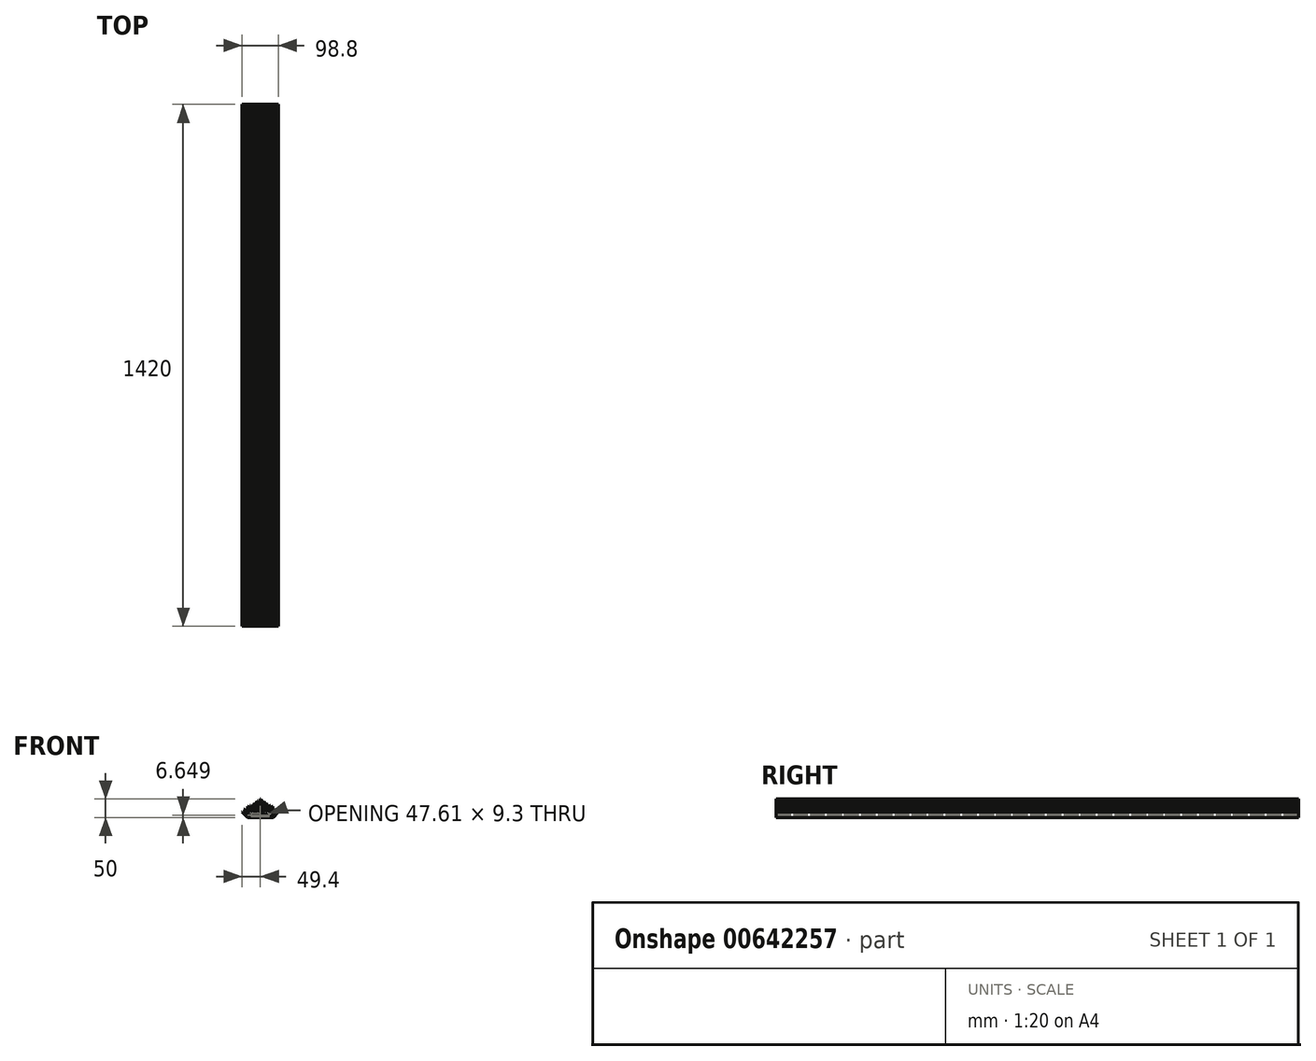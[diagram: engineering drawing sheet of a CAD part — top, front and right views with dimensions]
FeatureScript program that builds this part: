
annotation { "Feature Type Name" : "Feature", "Feature Type Description" : "" }
export const myFeature = defineFeature(function(context is Context, id is Id, definition is map)
    precondition{}
    {
        {
            var Q0;
            Q0=qCreatedBy(makeId("Front.planeOp"),FACE);
            var sketch = newSketch(context, id + "F0", { "sketchPlane" : qUnion([Q0])});
            skPoint(sketch, "E0.visualSharp", {"position": v(0, -3.5) * mm});
            skPoint(sketch, "E1.visualSharp", {"position": v(-32.72, 3.5) * mm});
            skLineSegment(sketch, "E2", {"start": v(-32.97, 18.5) * mm, "end": v(-34.47, 18.5) * mm});
            skLineSegment(sketch, "E3", {"start": v(-34.47, 18.5) * mm, "end": v(-34.72, 3.5) * mm});
            skLineSegment(sketch, "E4", {"start": v(-32.97, 18.5) * mm, "end": v(-32.72, 3.5) * mm});
            skLineSegment(sketch, "E5", {"start": v(-32.72, 3.5) * mm, "end": v(-28, 3.5) * mm});
            skLineSegment(sketch, "E6.1.0.0", {"start": v(-26.25, 21) * mm, "end": v(-26, 3.5) * mm});
            skLineSegment(sketch, "E6.1.0.2", {"start": v(-26, 3.5) * mm, "end": v(-21.24, 3.5) * mm});
            skPoint(sketch, "E6.1.0.3", {"position": v(-26, 3.5) * mm});
            skLineSegment(sketch, "E6.1.0.4", {"start": v(-26.25, 21) * mm, "end": v(-27.75, 21) * mm});
            skLineSegment(sketch, "E6.3.0.0", {"start": v(-12.87, 28.5) * mm, "end": v(-12.62, 3.5) * mm});
            skLineSegment(sketch, "E6.3.0.2", {"start": v(-12.62, 3.5) * mm, "end": v(-7.75, 3.5) * mm});
            skPoint(sketch, "E6.3.0.3", {"position": v(-12.62, 3.5) * mm});
            skLineSegment(sketch, "E6.3.0.4", {"start": v(-12.87, 28.5) * mm, "end": v(-14.37, 28.5) * mm});
            skLineSegment(sketch, "E6.4.0.0", {"start": v(-6, 33.5) * mm, "end": v(-5.75, 3.5) * mm});
            skLineSegment(sketch, "E6.4.0.2", {"start": v(-5.75, 3.5) * mm, "end": v(-1, 3.5) * mm});
            skPoint(sketch, "E6.4.0.3", {"position": v(-5.75, 3.5) * mm});
            skLineSegment(sketch, "E6.4.0.4", {"start": v(-6, 33.5) * mm, "end": v(-7.5, 33.5) * mm});
            skLineSegment(sketch, "E7", {"start": v(-27.75, 21) * mm, "end": v(-28, 3.5) * mm});
            skLineSegment(sketch, "E8", {"start": v(-20.99, 23.5) * mm, "end": v(-21.24, 3.5) * mm});
            skLineSegment(sketch, "E9", {"start": v(-0.75, 38.5) * mm, "end": v(-1, 3.5) * mm});
            skLineSegment(sketch, "E10", {"start": v(-7.75, 3.5) * mm, "end": v(-7.5, 33.5) * mm});
            skLineSegment(sketch, "E11", {"start": v(-14.37, 28.5) * mm, "end": v(-14.62, 3.5) * mm});
            skPoint(sketch, "E12", {"position": v(-34.72, 3.5) * mm});
            skLineSegment(sketch, "E13", {"start": v(0, -4.5) * mm, "end": v(-7.75, -4.5) * mm});
            skLineSegment(sketch, "E14", {"start": v(-34.72, 3.5) * mm, "end": v(-34.72, -11.5) * mm});
            skLineSegment(sketch, "E15", {"start": v(-7.75, -4.5) * mm, "end": v(-9.68, -2.2) * mm});
            skLineSegment(sketch, "E16", {"start": v(-11.21, -4.5) * mm, "end": v(-12.18, -3.35) * mm});
            skLineSegment(sketch, "E17", {"start": v(-28.55, -9) * mm, "end": v(-28.55, -7.5) * mm});
            skLineSegment(sketch, "E18", {"start": v(-28.55, -7.5) * mm, "end": v(-27.55, -7.5) * mm});
            skLineSegment(sketch, "E19", {"start": v(-25.3, -4.5) * mm, "end": v(-25.3, -9.5) * mm});
            skLineSegment(sketch, "E20", {"start": v(-23.8, -9.5) * mm, "end": v(-23.8, -4.5) * mm});
            skLineSegment(sketch, "E21.trimOffspring", {"start": v(-23.8, -4.5) * mm, "end": v(-11.21, -4.5) * mm});
            skLineSegment(sketch, "E22", {"start": v(-25.3, -4.5) * mm, "end": v(-27.72, -4.5) * mm});
            skLineSegment(sketch, "E23", {"start": v(-34.72, -11.5) * mm, "end": v(-27.55, -11.5) * mm});
            skLineSegment(sketch, "E24", {"start": v(-27.55, -7.5) * mm, "end": v(-27.55, -11.5) * mm});
            skLineSegment(sketch, "E25", {"start": v(-32.05, -7) * mm, "end": v(-32.05, -9) * mm});
            skLineSegment(sketch, "E26", {"start": v(-32.05, -9) * mm, "end": v(-28.55, -9) * mm});
            skLineSegment(sketch, "E27", {"start": v(-32.05, -7) * mm, "end": v(-27.72, -4.5) * mm});
            skLineSegment(sketch, "E28", {"start": v(-9.68, -2.2) * mm, "end": v(-9.68, -1.45) * mm});
            skLineSegment(sketch, "E29", {"start": v(-12.18, -3.35) * mm, "end": v(-12.18, -1.45) * mm});
            skArc(sketch, "E30", {"start": v(-9.68, -1.45) * mm, "mid": v(-10.93, -0.2) * mm, "end": v(-12.18, -1.45) * mm});
            skPoint(sketch, "E31", {"position": v(-19.24, 3.5) * mm});
            skLineSegment(sketch, "E32", {"start": v(-20.99, 23.5) * mm, "end": v(-19.49, 23.5) * mm});
            skLineSegment(sketch, "E33", {"start": v(-19.49, 23.5) * mm, "end": v(-19.24, 3.5) * mm});
            skLineSegment(sketch, "E34", {"start": v(-19.24, 3.5) * mm, "end": v(-14.62, 3.5) * mm});
            skLineSegment(sketch, "E35", {"start": v(-0.75, 38.5) * mm, "end": v(0, 38.5) * mm});
            skLineSegment(sketch, "E36", {"start": v(0, -4.5) * mm, "end": v(0, 38.5) * mm});
            skLineSegment(sketch, "E37", {"start": v(-27.1, -4.5) * mm, "end": v(-25.3, -4.5) * mm});
            skLineSegment(sketch, "E38", {"start": v(-25.3, -9.5) * mm, "end": v(-23.8, -9.5) * mm});
            skSolve(sketch);
        }
        {
            var Q0;
            Q0=qSketchRegion(id+"F0",true);
            extrude(context, id + "F1", {"entities" : qUnion([Q0]), "depth" : 1420 * mm, "offsetDistance" : 25 * mm});
        }
        {
            var Q0;
            Q0=makeQuery(id+"F1.opExtrude","CAP_FACE",FACE,{"disambiguationData":[OSD([sQuery(id+"F0.wireOp",EDGE,"E2"),sQuery(id+"F0.wireOp",EDGE,"E3"),sQuery(id+"F0.wireOp",EDGE,"E4"),sQuery(id+"F0.wireOp",EDGE,"E5"),sQuery(id+"F0.wireOp",EDGE,"E6.1.0.0"),sQuery(id+"F0.wireOp",EDGE,"E6.1.0.2"),sQuery(id+"F0.wireOp",EDGE,"E6.1.0.4"),sQuery(id+"F0.wireOp",EDGE,"E6.2.0.0"),sQuery(id+"F0.wireOp",EDGE,"E6.2.0.2"),sQuery(id+"F0.wireOp",EDGE,"E6.2.0.4"),sQuery(id+"F0.wireOp",EDGE,"E6.3.0.0"),sQuery(id+"F0.wireOp",EDGE,"E6.3.0.2"),sQuery(id+"F0.wireOp",EDGE,"E6.3.0.4"),sQuery(id+"F0.wireOp",EDGE,"E6.4.0.0"),sQuery(id+"F0.wireOp",EDGE,"E6.4.0.2"),sQuery(id+"F0.wireOp",EDGE,"E6.4.0.4"),sQuery(id+"F0.wireOp",EDGE,"E6.5.0.4"),sQuery(id+"F0.wireOp",EDGE,"E7"),sQuery(id+"F0.wireOp",EDGE,"E8"),sQuery(id+"F0.wireOp",EDGE,"E9"),sQuery(id+"F0.wireOp",EDGE,"E10"),sQuery(id+"F0.wireOp",EDGE,"E11"),sQuery(id+"F0.wireOp",EDGE,"6aw4rGms-xQcG-VMlr-JVcC-UaV8KcN4ZdL6"),sQuery(id+"F0.wireOp",EDGE,"E13"),sQuery(id+"F0.wireOp",EDGE,"E14"),sQuery(id+"F0.wireOp",EDGE,"E15"),sQuery(id+"F0.wireOp",EDGE,"E16"),sQuery(id+"F0.wireOp",EDGE,"B5nHTuO1-GDHi-FDC8-xcJy-4DZPArbVzKOm"),sQuery(id+"F0.wireOp",EDGE,"wrY0XtoE-YblG-YhcV-jUtB-XLkkbru2jkui"),sQuery(id+"F0.wireOp",EDGE,"pu7Z7fBI-ybBh-TTc0-hIZL-gMfkLwuN3Ia0"),sQuery(id+"F0.wireOp",EDGE,"GOzogHd3-TEJM-1mPt-nzWE-UlEZQVXn4zG3"),sQuery(id+"F0.wireOp",EDGE,"E17"),sQuery(id+"F0.wireOp",EDGE,"E18"),sQuery(id+"F0.wireOp",EDGE,"E19"),sQuery(id+"F0.wireOp",EDGE,"LJRGZIwq-aAv5-vMYT-1Wya-NWjgFLSVPvfh"),sQuery(id+"F0.wireOp",EDGE,"E20"),sQuery(id+"F0.wireOp",EDGE,"E21.trimOffspring"),sQuery(id+"F0.wireOp",EDGE,"E22"),sQuery(id+"F0.wireOp",EDGE,"E23"),sQuery(id+"F0.wireOp",EDGE,"E24"),sQuery(id+"F0.wireOp",EDGE,"j4S1P6x5-DvIn-s1OF-UvCF-FnaHhYbFjLOz"),sQuery(id+"F0.wireOp",EDGE,"dkx9Y0E6-F9Kh-A0fu-PcD4-sjYeOP9fUe4d")])],"isStart":false});
            var sketch = newSketch(context, id + "F2", { "sketchPlane" : qUnion([Q0])});
            skLineSegment(sketch, "E39", {"start": v(-34.72, 1) * mm, "end": v(-34.72, 3.5) * mm});
            skLineSegment(sketch, "E40", {"start": v(-34.72, 2.25) * mm, "end": v(-43.56, 11.09) * mm, "construction": true});
            skLineSegment(sketch, "E41", {"start": v(-43.03, 11.62) * mm, "end": v(-44.1, 10.56) * mm});
            skLineSegment(sketch, "E42", {"start": v(-43.03, 11.62) * mm, "end": v(-34.72, 3.5) * mm});
            skLineSegment(sketch, "E43", {"start": v(-44.1, 10.56) * mm, "end": v(-34.72, 1) * mm});
            skLineSegment(sketch, "E44", {"start": v(-34.72, -11.5) * mm, "end": v(-34.72, -9) * mm});
            skLineSegment(sketch, "E45", {"start": v(-34.72, -10.25) * mm, "end": v(-48.86, 3.9) * mm, "construction": true});
            skLineSegment(sketch, "E46", {"start": v(-48.33, 4.42) * mm, "end": v(-49.4, 3.36) * mm});
            skLineSegment(sketch, "E47", {"start": v(-48.33, 4.42) * mm, "end": v(-34.72, -9) * mm});
            skLineSegment(sketch, "E48", {"start": v(-49.4, 3.36) * mm, "end": v(-34.72, -11.5) * mm});
            skSolve(sketch);
        }
        {
            var Q0;
            Q0=qSketchRegion(id+"F2",true);
            extrude(context, id + "F3", {"entities" : qUnion([Q0]), "operationType" : NewBodyOperationType.ADD, "oppositeDirection" : true, "depth" : 1420 * mm, "offsetDistance" : 25 * mm});
        }
        {
            var Q0;
            {var subQ0=makeQuery(id+"F1.opExtrude","CAP_FACE",FACE,{"disambiguationData":[OSD([sQuery(id+"F0.wireOp",EDGE,"E2"),sQuery(id+"F0.wireOp",EDGE,"E3"),sQuery(id+"F0.wireOp",EDGE,"E4"),sQuery(id+"F0.wireOp",EDGE,"E5"),sQuery(id+"F0.wireOp",EDGE,"E6.1.0.0"),sQuery(id+"F0.wireOp",EDGE,"E6.1.0.2"),sQuery(id+"F0.wireOp",EDGE,"E6.1.0.4"),sQuery(id+"F0.wireOp",EDGE,"E6.3.0.0"),sQuery(id+"F0.wireOp",EDGE,"E6.3.0.2"),sQuery(id+"F0.wireOp",EDGE,"E6.3.0.4"),sQuery(id+"F0.wireOp",EDGE,"E6.4.0.0"),sQuery(id+"F0.wireOp",EDGE,"E6.4.0.2"),sQuery(id+"F0.wireOp",EDGE,"E6.4.0.4"),sQuery(id+"F0.wireOp",EDGE,"E7"),sQuery(id+"F0.wireOp",EDGE,"E8"),sQuery(id+"F0.wireOp",EDGE,"E9"),sQuery(id+"F0.wireOp",EDGE,"E10"),sQuery(id+"F0.wireOp",EDGE,"E11"),sQuery(id+"F0.wireOp",EDGE,"E13"),sQuery(id+"F0.wireOp",EDGE,"E14"),sQuery(id+"F0.wireOp",EDGE,"E15"),sQuery(id+"F0.wireOp",EDGE,"E16"),sQuery(id+"F0.wireOp",EDGE,"E17"),sQuery(id+"F0.wireOp",EDGE,"E18"),sQuery(id+"F0.wireOp",EDGE,"E19"),sQuery(id+"F0.wireOp",EDGE,"E20"),sQuery(id+"F0.wireOp",EDGE,"E21.trimOffspring"),sQuery(id+"F0.wireOp",EDGE,"E22"),sQuery(id+"F0.wireOp",EDGE,"E23"),sQuery(id+"F0.wireOp",EDGE,"E24"),sQuery(id+"F0.wireOp",EDGE,"E25"),sQuery(id+"F0.wireOp",EDGE,"E26"),sQuery(id+"F0.wireOp",EDGE,"E27"),sQuery(id+"F0.wireOp",EDGE,"E28"),sQuery(id+"F0.wireOp",EDGE,"E29"),sQuery(id+"F0.wireOp",EDGE,"E30"),sQuery(id+"F0.wireOp",EDGE,"E32"),sQuery(id+"F0.wireOp",EDGE,"E33"),sQuery(id+"F0.wireOp",EDGE,"E34"),sQuery(id+"F0.wireOp",EDGE,"E35"),sQuery(id+"F0.wireOp",EDGE,"E36"),sQuery(id+"F0.wireOp",EDGE,"E37"),sQuery(id+"F0.wireOp",EDGE,"E38")])],"isStart":false});Q0=makeQuery(id+"F6.boolean.opBoolean","MERGE",FACE,{"derivedFrom":[subQ0,makeQuery(id+"F6.opPattern","COPY",FACE,{"derivedFrom":subQ0,"instanceName":"1"})]});}
            var sketch = newSketch(context, id + "F4", { "sketchPlane" : qUnion([Q0])});
            skLineSegment(sketch, "E49", {"start": v(-25.3, -4.5) * mm, "end": v(-25.3, -9.5) * mm});
            skLineSegment(sketch, "E50", {"start": v(-25.3, -9.5) * mm, "end": v(0, -9.5) * mm});
            skLineSegment(sketch, "E51", {"start": v(0, -9.5) * mm, "end": v(0, -11.5) * mm});
            skLineSegment(sketch, "E52", {"start": v(0, -11.5) * mm, "end": v(-27.3, -11.5) * mm});
            skLineSegment(sketch, "E53", {"start": v(-27.3, -11.5) * mm, "end": v(-27.3, -4.5) * mm});
            skLineSegment(sketch, "E54", {"start": v(-27.3, -4.5) * mm, "end": v(-25.3, -4.5) * mm});
            skSolve(sketch);
        }
        {
            var Q0;
            Q0=qSketchRegion(id+"F4",true);
            extrude(context, id + "F5", {"entities" : qUnion([Q0]), "oppositeDirection" : true, "depth" : 1420 * mm, "offsetDistance" : 25 * mm});
        }
        {
            var Q0;
            Q0=makeQuery(id+"F1.opExtrude","SWEPT_BODY",BODY,{"disambiguationData":[OSD([sQuery(id+"F0.wireOp",EDGE,"E2"),sQuery(id+"F0.wireOp",EDGE,"E3"),sQuery(id+"F0.wireOp",EDGE,"E4"),sQuery(id+"F0.wireOp",EDGE,"E5"),sQuery(id+"F0.wireOp",EDGE,"E6.1.0.0"),sQuery(id+"F0.wireOp",EDGE,"E6.1.0.2"),sQuery(id+"F0.wireOp",EDGE,"E6.1.0.4"),sQuery(id+"F0.wireOp",EDGE,"E6.3.0.0"),sQuery(id+"F0.wireOp",EDGE,"E6.3.0.2"),sQuery(id+"F0.wireOp",EDGE,"E6.3.0.4"),sQuery(id+"F0.wireOp",EDGE,"E6.4.0.0"),sQuery(id+"F0.wireOp",EDGE,"E6.4.0.2"),sQuery(id+"F0.wireOp",EDGE,"E6.4.0.4"),sQuery(id+"F0.wireOp",EDGE,"E7"),sQuery(id+"F0.wireOp",EDGE,"E8"),sQuery(id+"F0.wireOp",EDGE,"E9"),sQuery(id+"F0.wireOp",EDGE,"E10"),sQuery(id+"F0.wireOp",EDGE,"E11"),sQuery(id+"F0.wireOp",EDGE,"E13"),sQuery(id+"F0.wireOp",EDGE,"E14"),sQuery(id+"F0.wireOp",EDGE,"E15"),sQuery(id+"F0.wireOp",EDGE,"E16"),sQuery(id+"F0.wireOp",EDGE,"E17"),sQuery(id+"F0.wireOp",EDGE,"E18"),sQuery(id+"F0.wireOp",EDGE,"E19"),sQuery(id+"F0.wireOp",EDGE,"LJRGZIwq-aAv5-vMYT-1Wya-NWjgFLSVPvfh"),sQuery(id+"F0.wireOp",EDGE,"E20"),sQuery(id+"F0.wireOp",EDGE,"E21.trimOffspring"),sQuery(id+"F0.wireOp",EDGE,"E22"),sQuery(id+"F0.wireOp",EDGE,"E23"),sQuery(id+"F0.wireOp",EDGE,"E24"),sQuery(id+"F0.wireOp",EDGE,"E25"),sQuery(id+"F0.wireOp",EDGE,"E26"),sQuery(id+"F0.wireOp",EDGE,"E27"),sQuery(id+"F0.wireOp",EDGE,"E28"),sQuery(id+"F0.wireOp",EDGE,"E29"),sQuery(id+"F0.wireOp",EDGE,"E30"),sQuery(id+"F0.wireOp",EDGE,"E32"),sQuery(id+"F0.wireOp",EDGE,"E33"),sQuery(id+"F0.wireOp",EDGE,"E34"),sQuery(id+"F0.wireOp",EDGE,"E35"),sQuery(id+"F0.wireOp",EDGE,"E36")])]});
            var Q1;
            Q1=makeQuery(id+"F1.opExtrude","SWEPT_BODY",BODY,{"disambiguationData":[OSD([sQuery(id+"F0.wireOp",EDGE,"9R7NK8zM-tC3Y-ZixV-HQ1Y-UdCP3e18fYu1"),sQuery(id+"F0.wireOp",EDGE,"hQkL2SHW-n77w-gf69-hCro-iTtwEbU04zFK"),sQuery(id+"F0.wireOp",EDGE,"g9Ot94Kp-ymDL-BriN-G1aE-UjGC9mEJR13i"),sQuery(id+"F0.wireOp",EDGE,"c3ti7Jjn-FzDr-I3oW-gQrF-BovdJvhkW4j7"),sQuery(id+"F0.wireOp",EDGE,"YMYXA4ls-wpxf-aHBe-Aeno-18cLMt04RpPS"),sQuery(id+"F0.wireOp",EDGE,"KmtUdOI4-E3le-O6Zy-3GTd-ahnRvYm0T2aJ")])]});
            var Q2;
            Q2=makeQuery(id+"F1.opExtrude","SWEPT_FACE",FACE,{"disambiguationData":[OSD([sQuery(id+"F0.wireOp",EDGE,"E36")])]});
            mirror(context, id + "F6", {"operationType" : NewBodyOperationType.ADD, "entities" : qUnion([Q0, Q1]), "mirrorPlane" : qUnion([Q2])});
        }
        {
            var Q0;
            Q0=makeQuery(id+"F5.opExtrude","SWEPT_BODY",BODY,{"disambiguationData":[OSD([sQuery(id+"F4.wireOp",EDGE,"E49"),sQuery(id+"F4.wireOp",EDGE,"E50"),sQuery(id+"F4.wireOp",EDGE,"E51"),sQuery(id+"F4.wireOp",EDGE,"E52"),sQuery(id+"F4.wireOp",EDGE,"E53"),sQuery(id+"F4.wireOp",EDGE,"E54")])]});
            var Q1;
            Q1=makeQuery(id+"F5.opExtrude","SWEPT_FACE",FACE,{"disambiguationData":[OSD([sQuery(id+"F4.wireOp",EDGE,"E51")])]});
            mirror(context, id + "F7", {"operationType" : NewBodyOperationType.ADD, "entities" : qUnion([Q0]), "mirrorPlane" : qUnion([Q1])});
        }
    });
